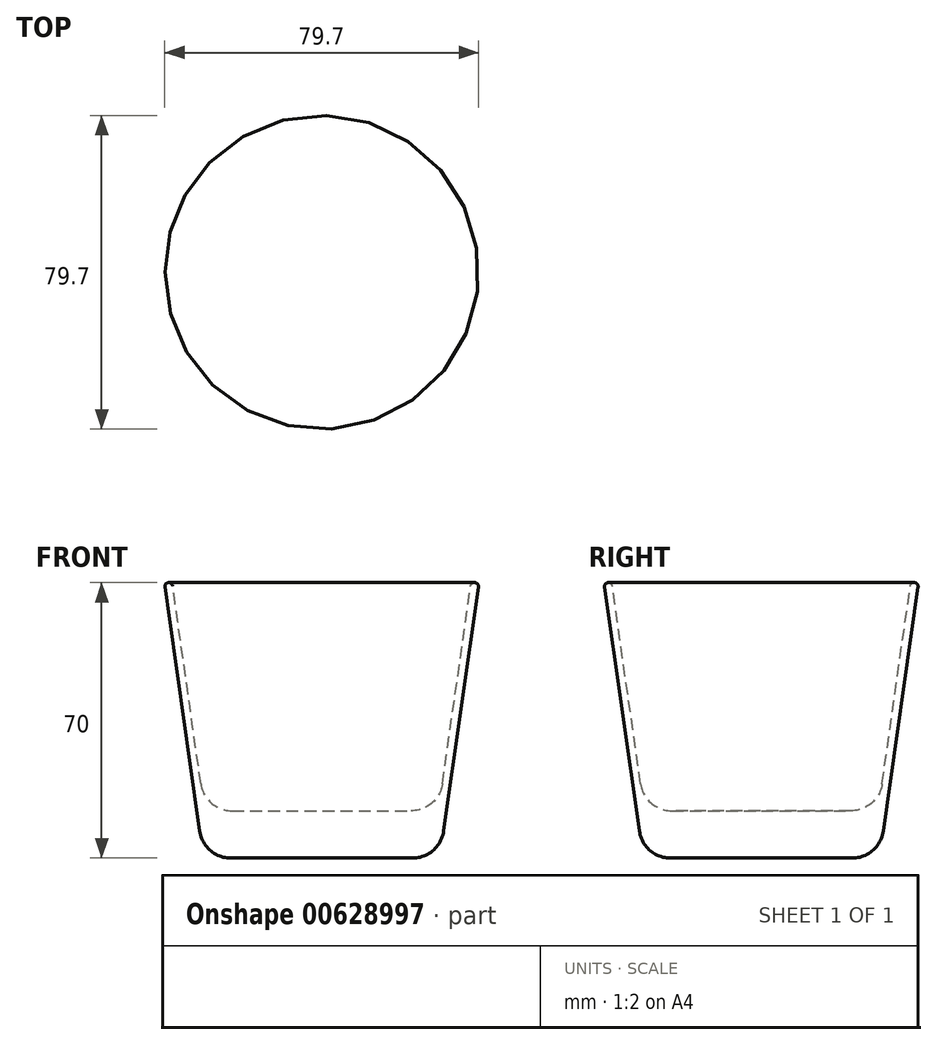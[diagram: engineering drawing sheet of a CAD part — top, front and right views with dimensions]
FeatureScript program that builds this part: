
annotation { "Feature Type Name" : "Feature", "Feature Type Description" : "" }
export const myFeature = defineFeature(function(context is Context, id is Id, definition is map)
    precondition{}
    {
        {
            var Q0;
            Q0=qCreatedBy(makeId("Front.planeOp"),FACE);
            var sketch = newSketch(context, id + "F0", { "sketchPlane" : qUnion([Q0])});
            skLineSegment(sketch, "E0", {"start": v(0, 0) * mm, "end": v(0, 91.6) * mm, "construction": true});
            skLineSegment(sketch, "E1", {"start": v(0, 0) * mm, "end": v(23.06, 0) * mm});
            skLineSegment(sketch, "E2", {"start": v(30.98, 6.87) * mm, "end": v(39.84, 68.86) * mm});
            skPoint(sketch, "E3.visualSharp", {"position": v(30, 0) * mm});
            skArc(sketch, "E3.filletArc", {"start": v(23.06, 0) * mm, "mid": v(28.3, 1.96) * mm, "end": v(30.98, 6.87) * mm});
            skLineSegment(sketch, "E4.0", {"start": v(30.68, 18.87) * mm, "end": v(37.86, 69.14) * mm});
            skLineSegment(sketch, "E5", {"start": v(0, 12) * mm, "end": v(22.76, 12) * mm});
            skArc(sketch, "E6.filletArc", {"start": v(22.76, 12) * mm, "mid": v(28, 13.96) * mm, "end": v(30.68, 18.87) * mm});
            skArc(sketch, "E7", {"start": v(39.84, 68.86) * mm, "mid": v(38.99, 69.99) * mm, "end": v(37.86, 69.14) * mm});
            skPoint(sketch, "E8.orphan", {"position": v(40, 70) * mm});
            skLineSegment(sketch, "E9", {"start": v(0, 12) * mm, "end": v(0, 0) * mm});
            skSolve(sketch);
        }
        {
            var Q0;
            Q0=makeQuery(id+"F0.imprint","IMPRINT",FACE,{"disambiguationData":[TD([[makeQuery(id+"F0.imprint","IMPRINT",EDGE,{"derivedFrom":sQuery(id+"F0.wireOp",EDGE,"E1")}),1.0]])]});
            var Q1;
            Q1=sQuery(id+"F0.wireOp",EDGE,"E0");
            revolve(context, id + "F1", {"entities" : qUnion([Q0]), "axis" : qUnion([Q1]), "revolveType" : RevolveType.FULL});
        }
    });
